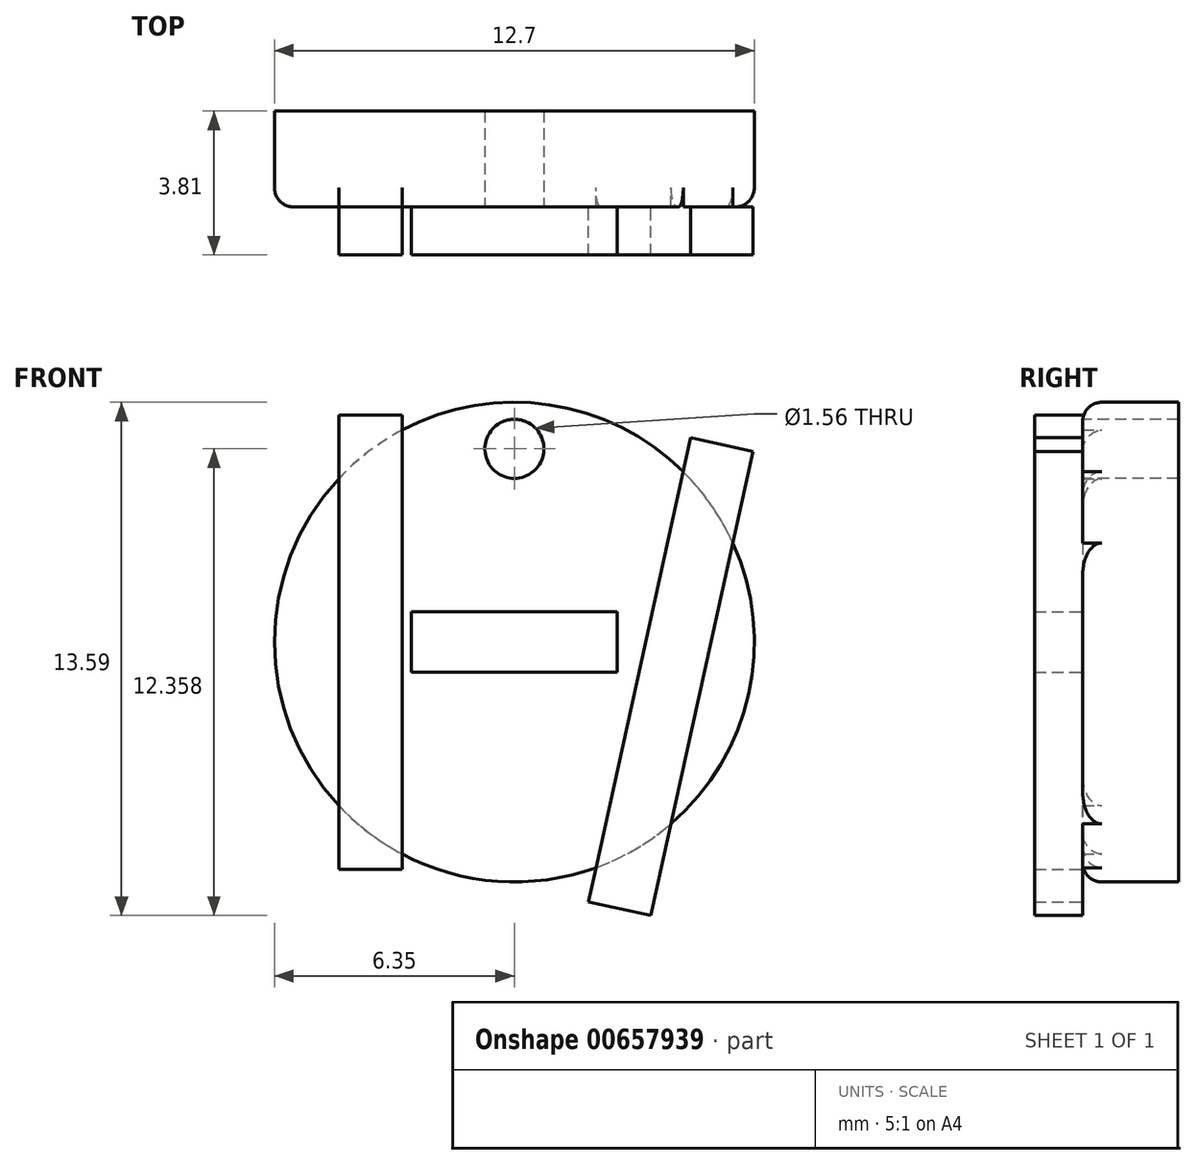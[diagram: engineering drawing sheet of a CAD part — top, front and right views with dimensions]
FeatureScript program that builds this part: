
annotation { "Feature Type Name" : "Feature", "Feature Type Description" : "" }
export const myFeature = defineFeature(function(context is Context, id is Id, definition is map)
    precondition{}
    {
        {
            var Q0;
            Q0=qCreatedBy(makeId("Front.planeOp"),FACE);
            var sketch = newSketch(context, id + "F0", { "sketchPlane" : qUnion([Q0])});
            skCircle(sketch, "E0", {"center": v(0, 0) * mm, "radius": 6.35 * mm});
            skSolve(sketch);
        }
        {
            var Q0;
            Q0 = qSketchRegion(id + "F0", true);
            extrude(context, id + "F1", {"entities" : qUnion([Q0]), "depth" : 2.54 * mm, "offsetDistance" : 25.4 * mm});
        }
        {
            var Q0;
            Q0=makeQuery(id+"F1.opExtrude","CAP_FACE",FACE,{"disambiguationData":[OSD([sQuery(id+"F0.wireOp",EDGE,"E0")])],"isStart":false});
            var sketch = newSketch(context, id + "F2", { "sketchPlane" : qUnion([Q0])});
            skLineSegment(sketch, "E1", {"start": v(-6.35, 0) * mm, "end": v(6.35, 0) * mm});
            skLineSegment(sketch, "E2.bottom", {"start": v(-2.97, -6.01) * mm, "end": v(-4.65, -6.01) * mm});
            skLineSegment(sketch, "E2.top", {"start": v(-2.97, 6.01) * mm, "end": v(-4.65, 6.01) * mm});
            skLineSegment(sketch, "E2.left", {"start": v(-2.97, -6.01) * mm, "end": v(-2.97, 6.01) * mm});
            skLineSegment(sketch, "E2.right", {"start": v(-4.65, -6.01) * mm, "end": v(-4.65, 6.01) * mm});
            skPoint(sketch, "E2.middle", {"position": v(-3.81, 0) * mm});
            skSolve(sketch);
        }
        {
            var Q0;
            Q0 = qSketchRegion(id + "F2", true);
            extrude(context, id + "F3", {"entities" : qUnion([Q0]), "operationType" : NewBodyOperationType.ADD, "depth" : 1.27 * mm, "offsetDistance" : 25.4 * mm});
        }
        {
            var Q0;
            {var subQ0=sQuery(id+"F0.wireOp",EDGE,"E0");var subQ1=sQuery(id+"F2.wireOp",EDGE,"E2.left");Q0=makeQuery(id+"F3.boolean.opBoolean","SPLIT",FACE,{"disambiguationData":[TD([makeQuery(id+"F3.opExtrude","SWEPT_FACE",FACE,{"disambiguationData":[OSD([subQ1])]})])],"derivedFrom":makeQuery(id+"F1.opExtrude","CAP_FACE",FACE,{"disambiguationData":[OSD([subQ0])],"isStart":false})});}
            var sketch = newSketch(context, id + "F4", { "sketchPlane" : qUnion([Q0])});
            skLineSegment(sketch, "E3", {"start": v(-6.3, 0) * mm, "end": v(6.35, 0) * mm});
            skLineSegment(sketch, "E4.bottom", {"start": v(2.72, 0.8) * mm, "end": v(-2.72, 0.8) * mm});
            skLineSegment(sketch, "E4.top", {"start": v(2.72, -0.8) * mm, "end": v(-2.72, -0.8) * mm});
            skLineSegment(sketch, "E4.left", {"start": v(2.72, 0.8) * mm, "end": v(2.72, -0.8) * mm});
            skLineSegment(sketch, "E4.right", {"start": v(-2.72, 0.8) * mm, "end": v(-2.72, -0.8) * mm});
            skPoint(sketch, "E4.middle", {"position": v(0, 0) * mm});
            skSolve(sketch);
        }
        {
            var Q0;
            Q0 = qSketchRegion(id + "F4", true);
            extrude(context, id + "F5", {"entities" : qUnion([Q0]), "operationType" : NewBodyOperationType.ADD, "depth" : 1.27 * mm, "offsetDistance" : 25.4 * mm});
        }
        {
            var Q0;
            {var subQ0=sQuery(id+"F0.wireOp",EDGE,"E0");var subQ1=sQuery(id+"F2.wireOp",EDGE,"E2.left");Q0=makeQuery(id+"F3.boolean.opBoolean","SPLIT",FACE,{"disambiguationData":[TD([makeQuery(id+"F3.opExtrude","SWEPT_FACE",FACE,{"disambiguationData":[OSD([subQ1])]})])],"derivedFrom":makeQuery(id+"F1.opExtrude","CAP_FACE",FACE,{"disambiguationData":[OSD([subQ0])],"isStart":false})});}
            var sketch = newSketch(context, id + "F6", { "sketchPlane" : qUnion([Q0])});
            skLineSegment(sketch, "E5", {"start": v(2.16, -5.97) * mm, "end": v(4.67, 5.41) * mm});
            skLineSegment(sketch, "E6", {"start": v(4.67, 5.41) * mm, "end": v(6.32, 5.05) * mm});
            skLineSegment(sketch, "E7", {"start": v(6.32, 5.05) * mm, "end": v(3.6, -7.24) * mm});
            skLineSegment(sketch, "E8", {"start": v(3.6, -7.24) * mm, "end": v(1.96, -6.88) * mm});
            skLineSegment(sketch, "E9", {"start": v(1.96, -6.88) * mm, "end": v(2.16, -5.97) * mm});
            skSolve(sketch);
        }
        {
            var Q0;
            Q0 = qSketchRegion(id + "F6", true);
            extrude(context, id + "F7", {"entities" : qUnion([Q0]), "operationType" : NewBodyOperationType.ADD, "depth" : 1.27 * mm, "offsetDistance" : 25.4 * mm});
        }
        {
            var Q0;
            {var subQ1=sQuery(id+"F2.wireOp",EDGE,"E2.left");var subQ2=makeQuery(id+"F3.opExtrude","SWEPT_FACE",FACE,{"disambiguationData":[OSD([subQ1])]});var subQ4=sQuery(id+"F0.wireOp",EDGE,"E0");Q0=makeQuery(id+"F7.boolean.opBoolean","SPLIT",FACE,{"disambiguationData":[TD([subQ2])],"derivedFrom":makeQuery(id+"F3.boolean.opBoolean","SPLIT",FACE,{"disambiguationData":[TD([subQ2])],"derivedFrom":makeQuery(id+"F1.opExtrude","CAP_FACE",FACE,{"disambiguationData":[OSD([subQ4])],"isStart":false})})});}
            var sketch = newSketch(context, id + "F8", { "sketchPlane" : qUnion([Q0])});
            skCircle(sketch, "E10", {"center": v(0, 5.12) * mm, "radius": 0.78 * mm});
            skSolve(sketch);
        }
        {
            var Q0;
            Q0 = qSketchRegion(id + "F8", true);
            extrude(context, id + "F9", {"entities" : qUnion([Q0]), "operationType" : NewBodyOperationType.REMOVE, "oppositeDirection" : true, "depth" : 25.4 * mm, "offsetDistance" : 25.4 * mm});
        }
        {
            var Q0;
            {var subQ0=sQuery(id+"F2.wireOp",EDGE,"E2.left");var subQ1=makeQuery(id+"F3.opExtrude","CAP_FACE",FACE,{"disambiguationData":[OSD([sQuery(id+"F2.wireOp",EDGE,"E2.bottom"),sQuery(id+"F2.wireOp",EDGE,"E2.top"),subQ0,sQuery(id+"F2.wireOp",EDGE,"E2.right")])],"isStart":true});var subQ2=sQuery(id+"F0.wireOp",EDGE,"E0");var subQ3=makeQuery(id+"F1.opExtrude","CAP_FACE",FACE,{"disambiguationData":[OSD([subQ2])],"isStart":false});var subQ4=makeQuery(id+"F3.opExtrude","SWEPT_FACE",FACE,{"disambiguationData":[OSD([subQ0])]});var subQ5=makeQuery(id+"F1.opExtrude","SWEPT_FACE",FACE,{"disambiguationData":[OSD([subQ2])]});var subQ6=sQuery(id+"F6.wireOp",EDGE,"E5");Q0=makeQuery(id+"F7.boolean.opBoolean","SPLIT",EDGE,{"disambiguationData":[topologyDisambiguationEdgeConnected([subQ5,subQ3]),TD([subQ5,subQ3,subQ1,subQ4,makeQuery(id+"F7.opExtrude","SWEPT_FACE",FACE,{"disambiguationData":[OSD([subQ6])]}),makeQuery(id+"F7.opExtrude","CAP_FACE",FACE,{"disambiguationData":[OSD([subQ6,sQuery(id+"F6.wireOp",EDGE,"E6"),sQuery(id+"F6.wireOp",EDGE,"E7"),sQuery(id+"F6.wireOp",EDGE,"E8"),sQuery(id+"F6.wireOp",EDGE,"E9")])],"isStart":true})])],"derivedFrom":makeQuery(id+"F3.boolean.opBoolean","SPLIT",EDGE,{"disambiguationData":[topologyDisambiguationEdgeConnected([subQ5,subQ3]),TD([subQ4])],"derivedFrom":makeQuery(id+"F1.opExtrude","CAP_EDGE",EDGE,{"disambiguationData":[OSD([subQ2])],"isStart":false})})});}
            fillet(context, id + "F10", {"entities" : qUnion([Q0]), "radius" : 0.5 * mm, "tangentPropagation" : true, "allowEdgeOverflow" : false});
        }
        {
            var Q0;
            {var subQ0=sQuery(id+"F0.wireOp",EDGE,"E0");var subQ1=makeQuery(id+"F1.opExtrude","SWEPT_FACE",FACE,{"disambiguationData":[OSD([subQ0])]});var subQ2=makeQuery(id+"F1.opExtrude","CAP_FACE",FACE,{"disambiguationData":[OSD([subQ0])],"isStart":false});var subQ3=sQuery(id+"F2.wireOp",EDGE,"E2.right");Q0=makeQuery(id+"F3.boolean.opBoolean","SPLIT",EDGE,{"disambiguationData":[topologyDisambiguationEdgeConnected([subQ1,subQ2]),TD([makeQuery(id+"F3.opExtrude","SWEPT_FACE",FACE,{"disambiguationData":[OSD([subQ3])]})])],"derivedFrom":makeQuery(id+"F1.opExtrude","CAP_EDGE",EDGE,{"disambiguationData":[OSD([subQ0])],"isStart":false})});}
            fillet(context, id + "F11", {"entities" : qUnion([Q0]), "radius" : 0.5 * mm, "tangentPropagation" : true, "allowEdgeOverflow" : false});
        }
        {
            var Q0;
            {var subQ0=sQuery(id+"F2.wireOp",EDGE,"E2.left");var subQ1=makeQuery(id+"F3.opExtrude","CAP_FACE",FACE,{"disambiguationData":[OSD([sQuery(id+"F2.wireOp",EDGE,"E2.bottom"),sQuery(id+"F2.wireOp",EDGE,"E2.top"),subQ0,sQuery(id+"F2.wireOp",EDGE,"E2.right")])],"isStart":true});var subQ2=sQuery(id+"F0.wireOp",EDGE,"E0");var subQ3=makeQuery(id+"F1.opExtrude","CAP_FACE",FACE,{"disambiguationData":[OSD([subQ2])],"isStart":false});var subQ4=makeQuery(id+"F3.opExtrude","SWEPT_FACE",FACE,{"disambiguationData":[OSD([subQ0])]});var subQ5=makeQuery(id+"F1.opExtrude","SWEPT_FACE",FACE,{"disambiguationData":[OSD([subQ2])]});var subQ6=sQuery(id+"F6.wireOp",EDGE,"E5");var subQ7=sQuery(id+"F6.wireOp",EDGE,"E9");Q0=makeQuery(id+"F7.boolean.opBoolean","SPLIT",EDGE,{"disambiguationData":[topologyDisambiguationEdgeConnected([subQ5,subQ3]),TD([subQ5,subQ3,subQ1,subQ4,makeQuery(id+"F7.opExtrude","SWEPT_FACE",FACE,{"disambiguationData":[OSD([subQ6])]}),makeQuery(id+"F7.opExtrude","CAP_FACE",FACE,{"disambiguationData":[OSD([subQ6,sQuery(id+"F6.wireOp",EDGE,"E6"),sQuery(id+"F6.wireOp",EDGE,"E7"),sQuery(id+"F6.wireOp",EDGE,"E8"),subQ7])],"isStart":true}),makeQuery(id+"F7.opExtrude","SWEPT_FACE",FACE,{"disambiguationData":[OSD([subQ7])]})])],"derivedFrom":makeQuery(id+"F3.boolean.opBoolean","SPLIT",EDGE,{"disambiguationData":[topologyDisambiguationEdgeConnected([subQ5,subQ3]),TD([subQ4])],"derivedFrom":makeQuery(id+"F1.opExtrude","CAP_EDGE",EDGE,{"disambiguationData":[OSD([subQ2])],"isStart":false})})});}
            fillet(context, id + "F12", {"entities" : qUnion([Q0]), "radius" : 0.5 * mm, "tangentPropagation" : true, "allowEdgeOverflow" : false});
        }
        {
            var Q0;
            {var subQ0=sQuery(id+"F0.wireOp",EDGE,"E0");var subQ1=makeQuery(id+"F1.opExtrude","SWEPT_FACE",FACE,{"disambiguationData":[OSD([subQ0])]});var subQ2=sQuery(id+"F6.wireOp",EDGE,"E7");var subQ3=makeQuery(id+"F1.opExtrude","CAP_FACE",FACE,{"disambiguationData":[OSD([subQ0])],"isStart":false});var subQ4=sQuery(id+"F2.wireOp",EDGE,"E2.left");Q0=makeQuery(id+"F7.boolean.opBoolean","SPLIT",EDGE,{"disambiguationData":[topologyDisambiguationEdgeConnected([subQ1,subQ3]),TD([subQ1,subQ3,makeQuery(id+"F7.opExtrude","CAP_FACE",FACE,{"disambiguationData":[OSD([sQuery(id+"F6.wireOp",EDGE,"E5"),sQuery(id+"F6.wireOp",EDGE,"E6"),subQ2,sQuery(id+"F6.wireOp",EDGE,"E8"),sQuery(id+"F6.wireOp",EDGE,"E9")])],"isStart":true}),makeQuery(id+"F7.opExtrude","SWEPT_FACE",FACE,{"disambiguationData":[OSD([subQ2])]})])],"derivedFrom":makeQuery(id+"F3.boolean.opBoolean","SPLIT",EDGE,{"disambiguationData":[topologyDisambiguationEdgeConnected([subQ1,subQ3]),TD([makeQuery(id+"F3.opExtrude","SWEPT_FACE",FACE,{"disambiguationData":[OSD([subQ4])]})])],"derivedFrom":makeQuery(id+"F1.opExtrude","CAP_EDGE",EDGE,{"disambiguationData":[OSD([subQ0])],"isStart":false})})});}
            fillet(context, id + "F13", {"entities" : qUnion([Q0]), "radius" : 0.5 * mm, "tangentPropagation" : true, "allowEdgeOverflow" : false});
        }
    });
